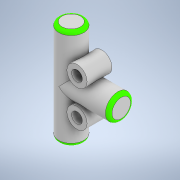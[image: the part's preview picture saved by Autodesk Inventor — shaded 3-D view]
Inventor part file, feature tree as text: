
AUTODESK INVENTOR PART (.ipt)
format: ipt  version: 2021 (Build 250183000, 183)  size: 174,592 bytes
history: native  units: mm
features: extrude x3, sketch x3, fillet x1, projected_geometry x1
ambient origin geometry x8: Origin, YZ Plane, XZ Plane, XY Plane, X Axis, Y Axis, Z Axis, Center Point
bodies: Solid1 (feature_tree)
feature tree (8):
  extrude  "Extrusion1"  Depth=29.8mm TaperAngle=0.0deg
  extrude  "Extrusion2"  Depth=14.9mm
  extrude  "Extrusion3"  Depth=1.0mm
  fillet  "Fillet1"  Radius=3.2mm
  sketch  "Sketch1"  dims[d0=7.5mm d1=29.8mm d2=0.0mm]
  sketch  "Sketch2"  dims[d3=14.9mm d4=0.0mm d5=5.4mm]
  projected_geometry  "Projected Loop1"
  sketch  "Sketch3"  dims[d6=5.4mm d7=3.2mm d8=3.2mm d9=6.0mm d10=6.0mm d11=5.4mm d12=5.4mm d13=7.4mm d14=0.0mm d15=1.0mm]
